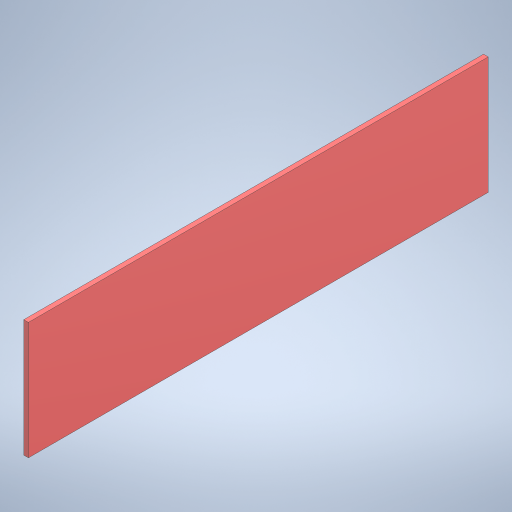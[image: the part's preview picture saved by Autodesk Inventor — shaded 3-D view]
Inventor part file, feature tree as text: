
AUTODESK INVENTOR PART (.ipt)
format: ipt  version: 2024.3 (Build 283343000, 343)  size: 196,096 bytes
history: native  units: mm
features: extrude x1, sketch x1
ambient origin geometry x8: Origin, YZ Plane, XZ Plane, XY Plane, X Axis, Y Axis, Z Axis, Center Point
bodies: Solid1 (feature_tree)
feature tree (2):
  extrude  "Extrusion1"  Depth=98.0mm
  sketch  "Sketch1"  dims[d0=25.0mm d1=98.0mm d2=1.0mm d3=0.0mm]
